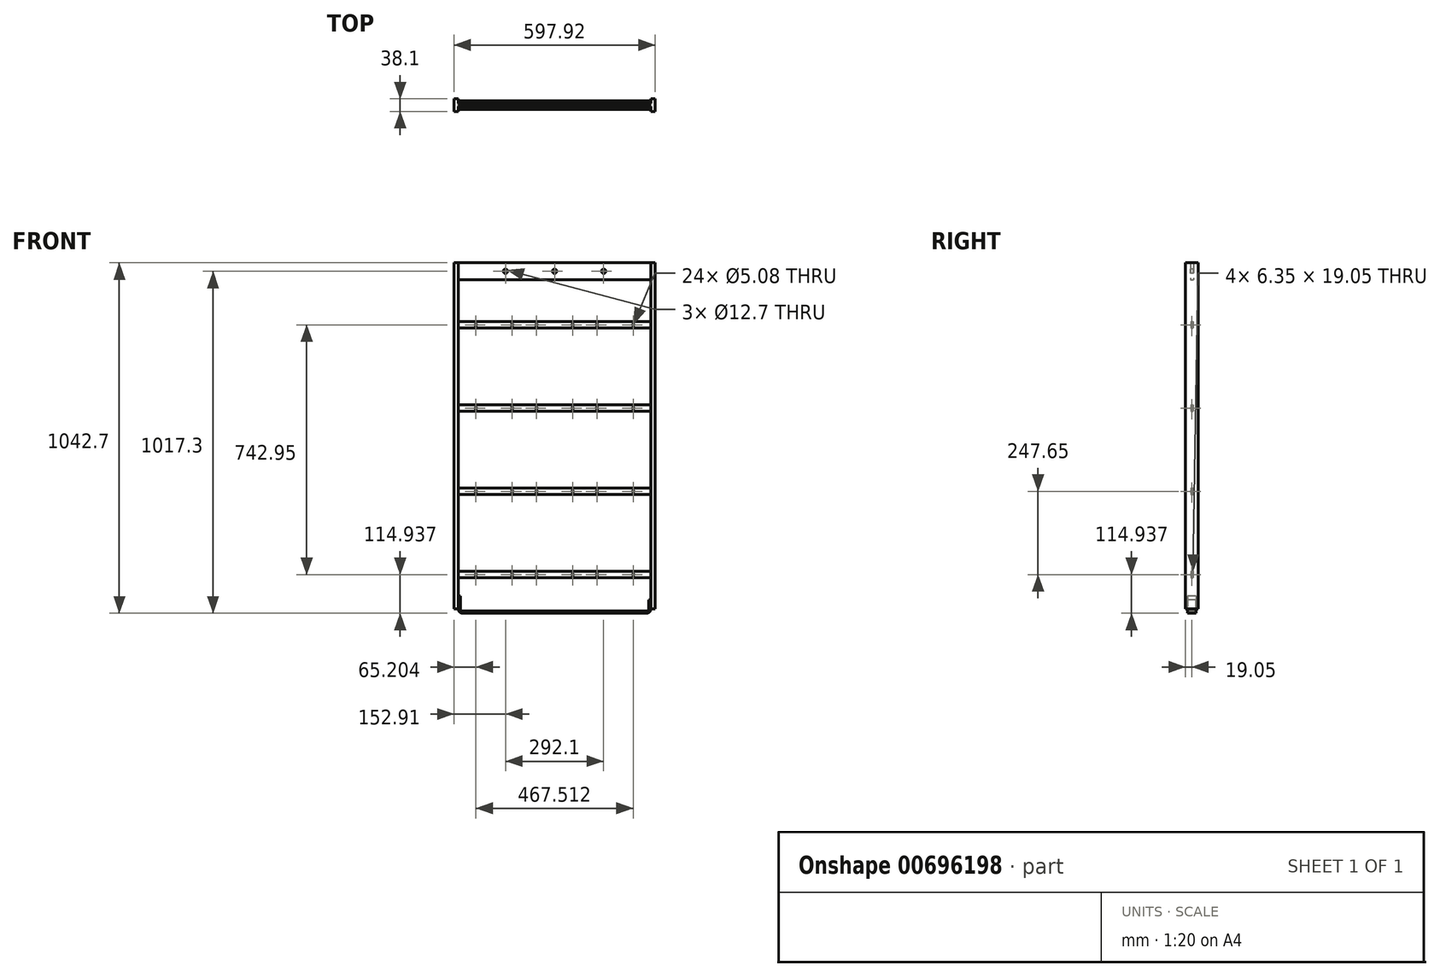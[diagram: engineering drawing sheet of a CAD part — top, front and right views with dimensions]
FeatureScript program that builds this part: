
annotation { "Feature Type Name" : "Feature", "Feature Type Description" : "" }
export const myFeature = defineFeature(function(context is Context, id is Id, definition is map)
    precondition{}
    {
        {
            var Q0;
            Q0=qCreatedBy(makeId("Front.planeOp"),FACE);
            var sketch = newSketch(context, id + "F0", { "sketchPlane" : qUnion([Q0])});
            skLineSegment(sketch, "E0", {"start": v(0, 487.25) * mm, "end": v(0, -485.6) * mm, "construction": true});
            skLineSegment(sketch, "E1", {"start": v(-474.86, 0) * mm, "end": v(451.74, 0) * mm, "construction": true});
            skPoint(sketch, "E2", {"position": v(0, 0) * mm});
            skLineSegment(sketch, "E3", {"start": v(-286.26, 515) * mm, "end": v(-286.26, 464.2) * mm});
            skLineSegment(sketch, "E4", {"start": v(-286.26, 464.2) * mm, "end": v(286.26, 464.2) * mm});
            skLineSegment(sketch, "E5", {"start": v(286.26, 464.2) * mm, "end": v(286.26, 515) * mm});
            skLineSegment(sketch, "E6", {"start": v(286.26, 515) * mm, "end": v(-286.26, 515) * mm});
            skLineSegment(sketch, "E7", {"start": v(-286.26, 515) * mm, "end": v(-298.96, 515) * mm});
            skLineSegment(sketch, "E8", {"start": v(-298.96, 515) * mm, "end": v(-298.96, -515) * mm});
            skLineSegment(sketch, "E9", {"start": v(-298.96, -515) * mm, "end": v(-286.26, -515) * mm});
            skLineSegment(sketch, "E10", {"start": v(-286.26, -515) * mm, "end": v(-286.26, 515) * mm});
            skLineSegment(sketch, "E11", {"start": v(286.26, 515) * mm, "end": v(298.96, 515) * mm});
            skLineSegment(sketch, "E12", {"start": v(298.96, 515) * mm, "end": v(298.96, -515) * mm});
            skLineSegment(sketch, "E13", {"start": v(298.96, -515) * mm, "end": v(286.26, -515) * mm});
            skLineSegment(sketch, "E14", {"start": v(286.26, -515) * mm, "end": v(286.26, 515) * mm});
            skSolve(sketch);
        }
        {
            var Q0;
            {var subQ0=sQuery(id+"F0.wireOp",EDGE,"E4");Q0=makeQuery(id+"F0.imprint","IMPRINT",FACE,{"disambiguationData":[TD([[makeQuery(id+"F0.imprint","IMPRINT",EDGE,{"derivedFrom":subQ0}),1.0]])]});}
            extrude(context, id + "F1", {"entities" : qUnion([Q0]), "endBound" : BoundingType.SYMMETRIC, "depth" : 9.12 * mm, "offsetDistance" : 25.4 * mm});
        }
        {
            var Q0;
            {var subQ3=sQuery(id+"F0.wireOp",EDGE,"E7");Q0=makeQuery(id+"F0.imprint","IMPRINT",FACE,{"disambiguationData":[TD([[makeQuery(id+"F0.imprint","IMPRINT",EDGE,{"derivedFrom":subQ3}),1.0]])]});}
            var Q1;
            {var subQ3=sQuery(id+"F0.wireOp",EDGE,"E11");Q1=makeQuery(id+"F0.imprint","IMPRINT",FACE,{"disambiguationData":[TD([[makeQuery(id+"F0.imprint","IMPRINT",EDGE,{"derivedFrom":subQ3}),-1.0]])]});}
            extrude(context, id + "F2", {"entities" : qUnion([Q0, Q1]), "operationType" : NewBodyOperationType.ADD, "endBound" : BoundingType.SYMMETRIC, "depth" : 38.1 * mm, "offsetDistance" : 25.4 * mm});
        }
        {
            var Q0;
            Q0=makeQuery(id+"F1.opExtrude","CAP_FACE",FACE,{"disambiguationData":[OSD([sQuery(id+"F0.wireOp",EDGE,"E4"),sQuery(id+"F0.wireOp",EDGE,"E6"),sQuery(id+"F0.wireOp",EDGE,"E10"),sQuery(id+"F0.wireOp",EDGE,"E14")])],"isStart":false});
            var sketch = newSketch(context, id + "F3", { "sketchPlane" : qUnion([Q0])});
            skPoint(sketch, "E15.endSnap0", {"position": v(286.26, 489.6) * mm});
            skLineSegment(sketch, "E16", {"start": v(146.05, 447.25) * mm, "end": v(-146.05, 447.25) * mm, "construction": true});
            skCircle(sketch, "E17", {"center": v(146.05, 489.6) * mm, "radius": 6.35 * mm});
            skCircle(sketch, "E18.1.0.0", {"center": v(0, 489.6) * mm, "radius": 6.35 * mm});
            skCircle(sketch, "E18.2.0.0", {"center": v(-146.05, 489.6) * mm, "radius": 6.35 * mm});
            skLineSegment(sketch, "E18.direction1", {"start": v(146.05, 489.6) * mm, "end": v(0, 489.6) * mm, "construction": true});
            skSolve(sketch);
        }
        {
            var Q0;
            Q0=makeQuery(id+"F3.imprint","IMPRINT",FACE,{"disambiguationData":[TD([[makeQuery(id+"F3.imprint","IMPRINT",EDGE,{"derivedFrom":sQuery(id+"F3.wireOp",EDGE,"E17")}),1.0]])]});
            var Q1;
            Q1=makeQuery(id+"F3.imprint","IMPRINT",FACE,{"disambiguationData":[TD([[makeQuery(id+"F3.imprint","IMPRINT",EDGE,{"derivedFrom":sQuery(id+"F3.wireOp",EDGE,"E18.2.0.0")}),1.0]])]});
            var Q2;
            Q2=makeQuery(id+"F3.imprint","IMPRINT",FACE,{"disambiguationData":[TD([[makeQuery(id+"F3.imprint","IMPRINT",EDGE,{"derivedFrom":sQuery(id+"F3.wireOp",EDGE,"E18.1.0.0")}),1.0]])]});
            extrude(context, id + "F4", {"entities" : qUnion([Q0, Q1, Q2]), "operationType" : NewBodyOperationType.REMOVE, "oppositeDirection" : true, "depth" : 25.4 * mm, "offsetDistance" : 25.4 * mm});
        }
        {
            var Q0;
            Q0=qCreatedBy(makeId("Front.planeOp"),FACE);
            var sketch = newSketch(context, id + "F5", { "sketchPlane" : qUnion([Q0])});
            skLineSegment(sketch, "E19", {"start": v(-286.3, -476.9) * mm, "end": v(-279.95, -476.9) * mm});
            skLineSegment(sketch, "E20", {"start": v(-279.95, -476.9) * mm, "end": v(-279.95, -515) * mm});
            skLineSegment(sketch, "E21", {"start": v(286.3, -487.99) * mm, "end": v(279.95, -487.99) * mm});
            skLineSegment(sketch, "E22", {"start": v(-273.6, -521.35) * mm, "end": v(273.6, -521.35) * mm});
            skLineSegment(sketch, "E23", {"start": v(279.95, -515) * mm, "end": v(279.95, -487.99) * mm});
            skPoint(sketch, "E24.visualSharp", {"position": v(-279.95, -521.35) * mm});
            skArc(sketch, "E24.filletArc", {"start": v(-279.95, -515) * mm, "mid": v(-278.09, -519.49) * mm, "end": v(-273.6, -521.35) * mm});
            skPoint(sketch, "E25.visualSharp", {"position": v(279.95, -521.35) * mm});
            skArc(sketch, "E25.filletArc", {"start": v(273.6, -521.35) * mm, "mid": v(278.09, -519.49) * mm, "end": v(279.95, -515) * mm});
            skLineSegment(sketch, "E26.0", {"start": v(286.3, -515) * mm, "end": v(286.3, -487.99) * mm});
            skLineSegment(sketch, "E26.1", {"start": v(-286.3, -476.9) * mm, "end": v(-286.3, -515) * mm});
            skArc(sketch, "E26.2", {"start": v(-286.3, -515) * mm, "mid": v(-282.58, -523.98) * mm, "end": v(-273.6, -527.7) * mm});
            skLineSegment(sketch, "E26.3", {"start": v(-273.6, -527.7) * mm, "end": v(273.6, -527.7) * mm});
            skArc(sketch, "E26.4", {"start": v(273.6, -527.7) * mm, "mid": v(282.58, -523.98) * mm, "end": v(286.3, -515) * mm});
            skSolve(sketch);
        }
        {
            var Q0;
            Q0=qCreatedBy(makeId("Front.planeOp"),FACE);
            var sketch = newSketch(context, id + "F6", { "sketchPlane" : qUnion([Q0])});
            skLineSegment(sketch, "E27", {"start": v(323.11, -515) * mm, "end": v(368.9, -515) * mm, "construction": true});
            skLineSegment(sketch, "E28", {"start": v(286.26, -403.24) * mm, "end": v(-286.26, -403.24) * mm});
            skLineSegment(sketch, "E29", {"start": v(-286.26, -403.24) * mm, "end": v(-286.26, -422.29) * mm});
            skLineSegment(sketch, "E30", {"start": v(-286.26, -422.29) * mm, "end": v(286.26, -422.29) * mm});
            skLineSegment(sketch, "E31", {"start": v(286.26, -422.29) * mm, "end": v(286.26, -403.24) * mm});
            skLineSegment(sketch, "E32.0.1.0", {"start": v(-286.26, -174.64) * mm, "end": v(286.26, -174.64) * mm});
            skLineSegment(sketch, "E32.0.1.1", {"start": v(286.26, -155.59) * mm, "end": v(-286.26, -155.59) * mm});
            skLineSegment(sketch, "E32.0.1.2", {"start": v(286.26, -174.64) * mm, "end": v(286.26, -155.59) * mm});
            skLineSegment(sketch, "E32.0.1.3", {"start": v(-286.26, -155.59) * mm, "end": v(-286.26, -174.64) * mm});
            skLineSegment(sketch, "E32.0.2.0", {"start": v(-286.26, 73.01) * mm, "end": v(286.26, 73.01) * mm});
            skLineSegment(sketch, "E32.0.2.1", {"start": v(286.26, 92.06) * mm, "end": v(-286.26, 92.06) * mm});
            skLineSegment(sketch, "E32.0.2.2", {"start": v(286.26, 73.01) * mm, "end": v(286.26, 92.06) * mm});
            skLineSegment(sketch, "E32.0.2.3", {"start": v(-286.26, 92.06) * mm, "end": v(-286.26, 73.01) * mm});
            skLineSegment(sketch, "E32.0.3.0", {"start": v(-286.26, 320.66) * mm, "end": v(286.26, 320.66) * mm});
            skLineSegment(sketch, "E32.0.3.1", {"start": v(286.26, 339.71) * mm, "end": v(-286.26, 339.71) * mm});
            skLineSegment(sketch, "E32.0.3.2", {"start": v(286.26, 320.66) * mm, "end": v(286.26, 339.71) * mm});
            skLineSegment(sketch, "E32.0.3.3", {"start": v(-286.26, 339.71) * mm, "end": v(-286.26, 320.66) * mm});
            skLineSegment(sketch, "E32.direction1", {"start": v(-286.26, -422.29) * mm, "end": v(-260.86, -422.29) * mm, "construction": true});
            skLineSegment(sketch, "E32.direction2", {"start": v(-286.26, -422.29) * mm, "end": v(-286.26, -174.64) * mm, "construction": true});
            skCircle(sketch, "E33", {"center": v(233.76, -412.76) * mm, "radius": 2.54 * mm});
            skPoint(sketch, "E33.centerSnap0", {"position": v(286.26, -412.76) * mm});
            skCircle(sketch, "E34", {"center": v(126.26, -412.76) * mm, "radius": 2.54 * mm});
            skCircle(sketch, "E35.1.0.0", {"center": v(53.75, -412.76) * mm, "radius": 2.54 * mm});
            skCircle(sketch, "E35.2.0.0", {"center": v(-126.26, -412.76) * mm, "radius": 2.54 * mm});
            skLineSegment(sketch, "E35.direction1", {"start": v(233.76, -412.76) * mm, "end": v(53.75, -412.76) * mm, "construction": true});
            skCircle(sketch, "E36.1.0.0", {"center": v(-53.75, -412.76) * mm, "radius": 2.54 * mm});
            skCircle(sketch, "E36.2.0.0", {"center": v(-233.76, -412.76) * mm, "radius": 2.54 * mm});
            skLineSegment(sketch, "E36.direction1", {"start": v(126.26, -412.76) * mm, "end": v(-53.75, -412.76) * mm, "construction": true});
            skCircle(sketch, "E37.0.1.0", {"center": v(233.76, -165.11) * mm, "radius": 2.54 * mm});
            skCircle(sketch, "E37.0.1.1", {"center": v(126.26, -165.11) * mm, "radius": 2.54 * mm});
            skCircle(sketch, "E37.0.1.2", {"center": v(53.75, -165.11) * mm, "radius": 2.54 * mm});
            skCircle(sketch, "E37.0.1.3", {"center": v(-53.75, -165.11) * mm, "radius": 2.54 * mm});
            skCircle(sketch, "E37.0.1.4", {"center": v(-126.26, -165.11) * mm, "radius": 2.54 * mm});
            skCircle(sketch, "E37.0.1.5", {"center": v(-233.76, -165.11) * mm, "radius": 2.54 * mm});
            skCircle(sketch, "E37.0.2.0", {"center": v(233.76, 82.54) * mm, "radius": 2.54 * mm});
            skCircle(sketch, "E37.0.2.1", {"center": v(126.26, 82.54) * mm, "radius": 2.54 * mm});
            skCircle(sketch, "E37.0.2.2", {"center": v(53.75, 82.54) * mm, "radius": 2.54 * mm});
            skCircle(sketch, "E37.0.2.3", {"center": v(-53.75, 82.54) * mm, "radius": 2.54 * mm});
            skCircle(sketch, "E37.0.2.4", {"center": v(-126.26, 82.54) * mm, "radius": 2.54 * mm});
            skCircle(sketch, "E37.0.2.5", {"center": v(-233.76, 82.54) * mm, "radius": 2.54 * mm});
            skCircle(sketch, "E37.0.3.0", {"center": v(233.76, 330.19) * mm, "radius": 2.54 * mm});
            skCircle(sketch, "E37.0.3.1", {"center": v(126.26, 330.19) * mm, "radius": 2.54 * mm});
            skCircle(sketch, "E37.0.3.2", {"center": v(53.75, 330.19) * mm, "radius": 2.54 * mm});
            skCircle(sketch, "E37.0.3.3", {"center": v(-53.75, 330.19) * mm, "radius": 2.54 * mm});
            skCircle(sketch, "E37.0.3.4", {"center": v(-126.26, 330.19) * mm, "radius": 2.54 * mm});
            skCircle(sketch, "E37.0.3.5", {"center": v(-233.76, 330.19) * mm, "radius": 2.54 * mm});
            skLineSegment(sketch, "E37.direction1", {"start": v(-233.76, -412.76) * mm, "end": v(-208.36, -412.76) * mm, "construction": true});
            skLineSegment(sketch, "E37.direction2", {"start": v(-233.76, -412.76) * mm, "end": v(-233.76, -165.11) * mm, "construction": true});
            skSolve(sketch);
        }
        {
            var Q0;
            Q0=makeQuery(id+"F6.imprint","IMPRINT",FACE,{"disambiguationData":[TD([[makeQuery(id+"F6.imprint","IMPRINT",EDGE,{"derivedFrom":sQuery(id+"F6.wireOp",EDGE,"E28")}),1.0]])]});
            var Q1;
            Q1=makeQuery(id+"F6.imprint","IMPRINT",FACE,{"disambiguationData":[TD([[makeQuery(id+"F6.imprint","IMPRINT",EDGE,{"derivedFrom":sQuery(id+"F6.wireOp",EDGE,"E32.0.1.0")}),1.0]])]});
            var Q2;
            Q2=makeQuery(id+"F6.imprint","IMPRINT",FACE,{"disambiguationData":[TD([[makeQuery(id+"F6.imprint","IMPRINT",EDGE,{"derivedFrom":sQuery(id+"F6.wireOp",EDGE,"E32.0.2.0")}),1.0]])]});
            var Q3;
            Q3=makeQuery(id+"F6.imprint","IMPRINT",FACE,{"disambiguationData":[TD([[makeQuery(id+"F6.imprint","IMPRINT",EDGE,{"derivedFrom":sQuery(id+"F6.wireOp",EDGE,"E32.0.3.0")}),1.0]])]});
            extrude(context, id + "F7", {"entities" : qUnion([Q0, Q1, Q2, Q3]), "operationType" : NewBodyOperationType.ADD, "endBound" : BoundingType.SYMMETRIC, "depth" : 6.35 * mm, "offsetDistance" : 25.4 * mm});
        }
        {
            var Q0;
            Q0=makeQuery(id+"F5.imprint","IMPRINT",FACE,{"disambiguationData":[TD([[makeQuery(id+"F5.imprint","IMPRINT",EDGE,{"derivedFrom":sQuery(id+"F5.wireOp",EDGE,"E19")}),-1.0]])]});
            extrude(context, id + "F8", {"entities" : qUnion([Q0]), "operationType" : NewBodyOperationType.ADD, "endBound" : BoundingType.SYMMETRIC, "depth" : 25.4 * mm, "offsetDistance" : 25.4 * mm});
        }
    });
